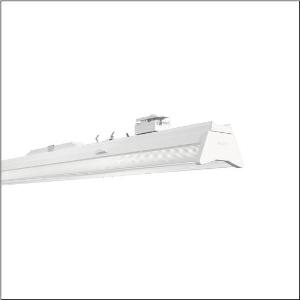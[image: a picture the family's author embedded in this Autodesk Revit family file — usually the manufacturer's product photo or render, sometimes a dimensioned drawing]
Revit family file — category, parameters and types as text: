
# Revit family: licross_21_performance_mo_52tm167n445g
name_source: partatom
category: Lighting Fixtures
units: mm (PartAtom-declared; Revit-internal decimal feet)

## family parameters
Cut with Voids When Loaded = No
Host = Face
Light Source = No
Part Type = Normal
Room Calculation Point = No
Round Connector Dimension = Use Diameter
Shared = No

## types (1)
- Licross 21 Performance MO (1 x LED, 4580 lm, 24.7 W, 4000K)
    Apparent Load = 25 VA
    CIE Flux Codes = 66 88 96 79 100
    Color Rendering = 80
    Color Temperature = 4000K
    Default Elevation = 1800 mm
    Description = Licross 21 Performance MO, luminaire insert, of sheet steel, galvanised, coil coated, white, length: 1.500mm, width: 120mm, height: 123mm, LED rated luminous flux: 4.580lm, light colour: 840, SDCM (Standard Deviation of Colour Matching)MacAdam ≤ 3 SDCM (initial), control gear: ON/OFF, with plug, 3-pole, with phase selection, mains connection: 220..240V, AC, 50/60Hz, rated input power: 25W, internal wiring halogen-free, primary light control with lens, of plastic, primary optical cover: cover, of PMMA, CAT 2 (L<= 3000cd/m²), light emission: direct/indirect distribution, primary light characteristic: symmetric, protection rating (complete): IP40, insulation class (complete): insulation class I (protective earthing), certification: CE, ENEC, UKCA, protection symbol: D if used in an environment without relevant dust loads with corresponding accessories, impact resistance: IK06, permissible ambient temperature for indoor applications: -35..+55°C, corresponds to IFS (International Featured Standards) requirements for safety and quality in the food industry, reducing of maximum allowable ambient temperature of 5°C with ceiling mounting, LABS conformity tested according to VDMA 24364:2018-05, The light source and the operating device comply with the requirements of the Ecodesign Regulation (EU) 2019/2020 and are replaceable in accordance with this regulation, packaging unit: 1 piece
    Height = 114 mm
    Lamp = 1 x LED
    Lamp Light Flux = 4580 lm
    Lamp Power = 24.7 W
    Lamp count = 1
    Length = 1500 mm
    Luminous efficacy = 185 lm/W
    Manufacturer = Siteco
    ModVariant = No
    Model = 52TM167N445G
    Mounting Place = Ceiling
    Mounting Type = Pendant
    Number of Poles = 1
    OnlyDefault = Yes
    Power Factor = 1
    Product Name = Licross 21 Performance MO
    Product group = luminaire insert | ceiling pendant
    ProductGroupID = 901
    Protection Class = Protection class I
    Protection Degree = IP 40
    RLX_Detail_Level = 1
    RLX_Emergency_Light_Flux = 0 lm
    RLX_Emergency_Type = 0
    RLX_Emergency_Type_DB = No
    RlxData = <blob elided: 30693 chars, md5=cbe2b976>
    Socket = socket
    Standby Power = 0 W
    System Light Flux = 4580 lm
    System Power = 25 W
    Type Comments = Product without accessories
    Type Image = l_1256138.jpg
    URL = http://relux.com
    VarID = ---
    Voltage = 0 V
    Weight = 0.00 kg
    Width = 120 mm

## geometry (parser evidence)
native form markers: Blend x4, Sweep x14
no freeform markers — native parametric forms only
